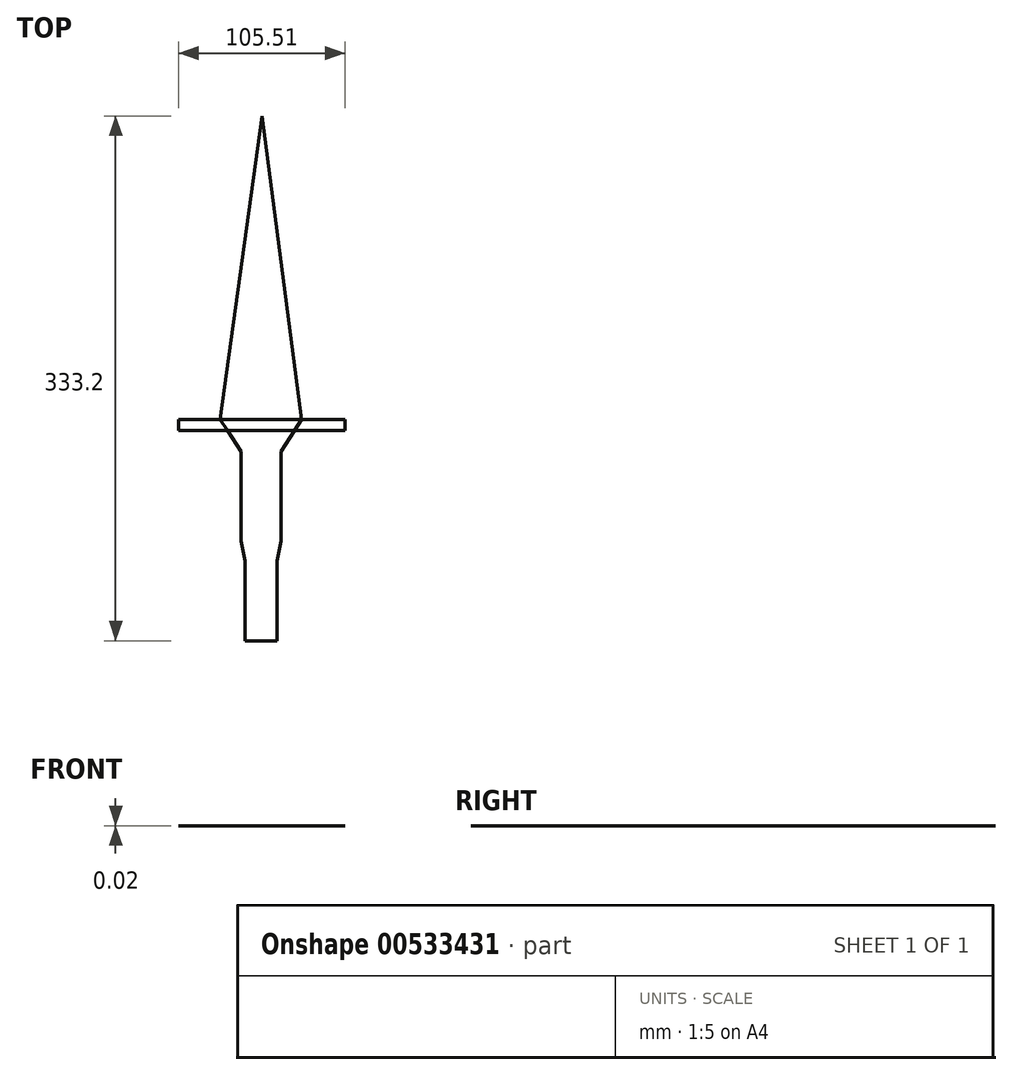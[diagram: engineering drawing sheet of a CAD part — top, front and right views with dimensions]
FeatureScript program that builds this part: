
annotation { "Feature Type Name" : "Feature", "Feature Type Description" : "" }
export const myFeature = defineFeature(function(context is Context, id is Id, definition is map)
    precondition{}
    {
        {
            var Q0;
            Q0=qCreatedBy(makeId("Top.planeOp"),FACE);
            var sketch = newSketch(context, id + "F0", { "sketchPlane" : qUnion([Q0])});
            skLineSegment(sketch, "E0", {"start": v(0, 0) * mm, "end": v(0, 192.53) * mm});
            skLineSegment(sketch, "E1", {"start": v(0, 192.53) * mm, "end": v(-26.38, 0) * mm});
            skLineSegment(sketch, "E2", {"start": v(0, 192.53) * mm, "end": v(25.21, 0) * mm});
            skLineSegment(sketch, "E3", {"start": v(-26.38, 0) * mm, "end": v(0, 0) * mm});
            skLineSegment(sketch, "E4", {"start": v(25.21, 0) * mm, "end": v(0, 0) * mm});
            skLineSegment(sketch, "E5", {"start": v(0, 0) * mm, "end": v(52.75, 0) * mm});
            skLineSegment(sketch, "E6", {"start": v(0, 0) * mm, "end": v(-52.76, 0) * mm});
            skLineSegment(sketch, "E7", {"start": v(-52.76, 0) * mm, "end": v(-52.76, -7.1) * mm});
            skLineSegment(sketch, "E8", {"start": v(-52.76, -7.1) * mm, "end": v(52.75, -7.1) * mm});
            skLineSegment(sketch, "E9", {"start": v(52.75, -7.1) * mm, "end": v(52.75, 0) * mm});
            skLineSegment(sketch, "E10", {"start": v(-26.38, 0) * mm, "end": v(-13.2, -20.46) * mm});
            skPoint(sketch, "E10.endSnap0", {"position": v(-13.2, 0) * mm});
            skLineSegment(sketch, "E11", {"start": v(25.21, 0) * mm, "end": v(12.36, -20.46) * mm});
            skLineSegment(sketch, "E12", {"start": v(12.36, -20.46) * mm, "end": v(-13.2, -20.46) * mm});
            skLineSegment(sketch, "E13", {"start": v(-13.2, -20.46) * mm, "end": v(-13.2, -77.17) * mm});
            skLineSegment(sketch, "E14", {"start": v(-13.2, -77.17) * mm, "end": v(12.36, -77.17) * mm});
            skLineSegment(sketch, "E15", {"start": v(12.36, -20.46) * mm, "end": v(12.36, -77.17) * mm});
            skPoint(sketch, "E16.end.orphan", {"position": v(0, -90.93) * mm});
            skPoint(sketch, "E17.end.orphan", {"position": v(10.17, -128.7) * mm});
            skPoint(sketch, "E18.end.orphan", {"position": v(10.17, -90.93) * mm});
            skLineSegment(sketch, "E19", {"start": v(9.82, -89.87) * mm, "end": v(12.36, -77.17) * mm});
            skLineSegment(sketch, "E20", {"start": v(-13.2, -77.17) * mm, "end": v(-10.65, -89.87) * mm});
            skPoint(sketch, "E21.end.orphan", {"position": v(0, -128.78) * mm});
            skLineSegment(sketch, "E22", {"start": v(9.82, -89.87) * mm, "end": v(9.82, -140.67) * mm});
            skLineSegment(sketch, "E23", {"start": v(-10.65, -89.87) * mm, "end": v(-10.65, -140.67) * mm});
            skLineSegment(sketch, "E24", {"start": v(-10.65, -140.67) * mm, "end": v(9.82, -140.67) * mm});
            skSolve(sketch);
        }
        {
            var Q0;
            {var subQ0=sQuery(id+"F0.wireOp",EDGE,"E0");Q0=makeQuery(id+"F0.imprint","IMPRINT",FACE,{"disambiguationData":[TD([[makeQuery(id+"F0.imprint","IMPRINT",EDGE,{"derivedFrom":subQ0}),-1.0]])]});}
            var Q1;
            {var subQ0=sQuery(id+"F0.wireOp",EDGE,"E0");Q1=makeQuery(id+"F0.imprint","IMPRINT",FACE,{"disambiguationData":[TD([[makeQuery(id+"F0.imprint","IMPRINT",EDGE,{"derivedFrom":subQ0}),1.0]])]});}
            extrude(context, id + "F1", {"entities" : qUnion([Q0, Q1]), "depth" : 1 / 406.4 * mm, "offsetDistance" : 25.4 * mm});
        }
        {
            var Q0;
            {var subQ3=sQuery(id+"F0.wireOp",EDGE,"E9");Q0=makeQuery(id+"F0.imprint","IMPRINT",FACE,{"disambiguationData":[TD([[makeQuery(id+"F0.imprint","IMPRINT",EDGE,{"derivedFrom":subQ3}),1.0]])]});}
            var Q1;
            {var subQ3=sQuery(id+"F0.wireOp",EDGE,"E7");Q1=makeQuery(id+"F0.imprint","IMPRINT",FACE,{"disambiguationData":[TD([[makeQuery(id+"F0.imprint","IMPRINT",EDGE,{"derivedFrom":subQ3}),1.0]])]});}
            extrude(context, id + "F2", {"entities" : qUnion([Q0, Q1]), "depth" : 1 / 101.6 * mm, "offsetDistance" : 25.4 * mm});
        }
        {
            var Q0;
            {var subQ0=sQuery(id+"F0.wireOp",EDGE,"E10");var subQ3=sQuery(id+"F0.wireOp",EDGE,"E8");var subQ4=makeQuery(id+"F0.imprint","INTERSECT",VERTEX,{"derivedFrom":[subQ3,subQ0]});Q0=makeQuery(id+"F0.imprint","IMPRINT",FACE,{"disambiguationData":[TD([[makeQuery(id+"F0.imprint","IMPRINT",EDGE,{"disambiguationData":[TD([[subQ4,-1.0]])],"derivedFrom":subQ3}),1.0]])]});}
            extrude(context, id + "F3", {"entities" : qUnion([Q0]), "depth" : 1 / 50.8 * mm, "offsetDistance" : 25.4 * mm});
        }
        {
            var Q0;
            Q0=makeQuery(id+"F0.imprint","IMPRINT",FACE,{"disambiguationData":[TD([[makeQuery(id+"F0.imprint","IMPRINT",EDGE,{"derivedFrom":sQuery(id+"F0.wireOp",EDGE,"E14")}),-1.0]])]});
            var Q1;
            Q1=makeQuery(id+"F0.imprint","IMPRINT",FACE,{"disambiguationData":[TD([[makeQuery(id+"F0.imprint","IMPRINT",EDGE,{"derivedFrom":sQuery(id+"F0.wireOp",EDGE,"E12")}),1.0]])]});
            var Q2;
            {var subQ5=sQuery(id+"F0.wireOp",EDGE,"E12");Q2=makeQuery(id+"F0.imprint","IMPRINT",FACE,{"disambiguationData":[TD([[makeQuery(id+"F0.imprint","IMPRINT",EDGE,{"derivedFrom":subQ5}),-1.0]])]});}
            extrude(context, id + "F4", {"entities" : qUnion([Q0, Q1, Q2]), "operationType" : NewBodyOperationType.ADD, "depth" : 1 / 203.2 * mm, "offsetDistance" : 25.4 * mm});
        }
    });
